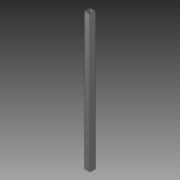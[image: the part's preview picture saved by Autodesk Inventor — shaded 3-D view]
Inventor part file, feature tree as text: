
AUTODESK INVENTOR PART (.ipt)
format: ipt  version: 2019 (Build 230136000, 136)  size: 81,408 bytes
history: native  units: mm
features: extrude x1, sketch x1
ambient origin geometry x8: Origin, YZ Plane, XZ Plane, XY Plane, X Axis, Y Axis, Z Axis, Center Point
bodies: Solid1 (feature_tree)
feature tree (2):
  extrude  "Extrusion1"  Depth=30.0mm
  sketch  "Sketch1"  dims[d0=30.0mm d1=30.0mm d2=2.5mm d3=2.5mm d4=750.0mm d5=0.0mm]
